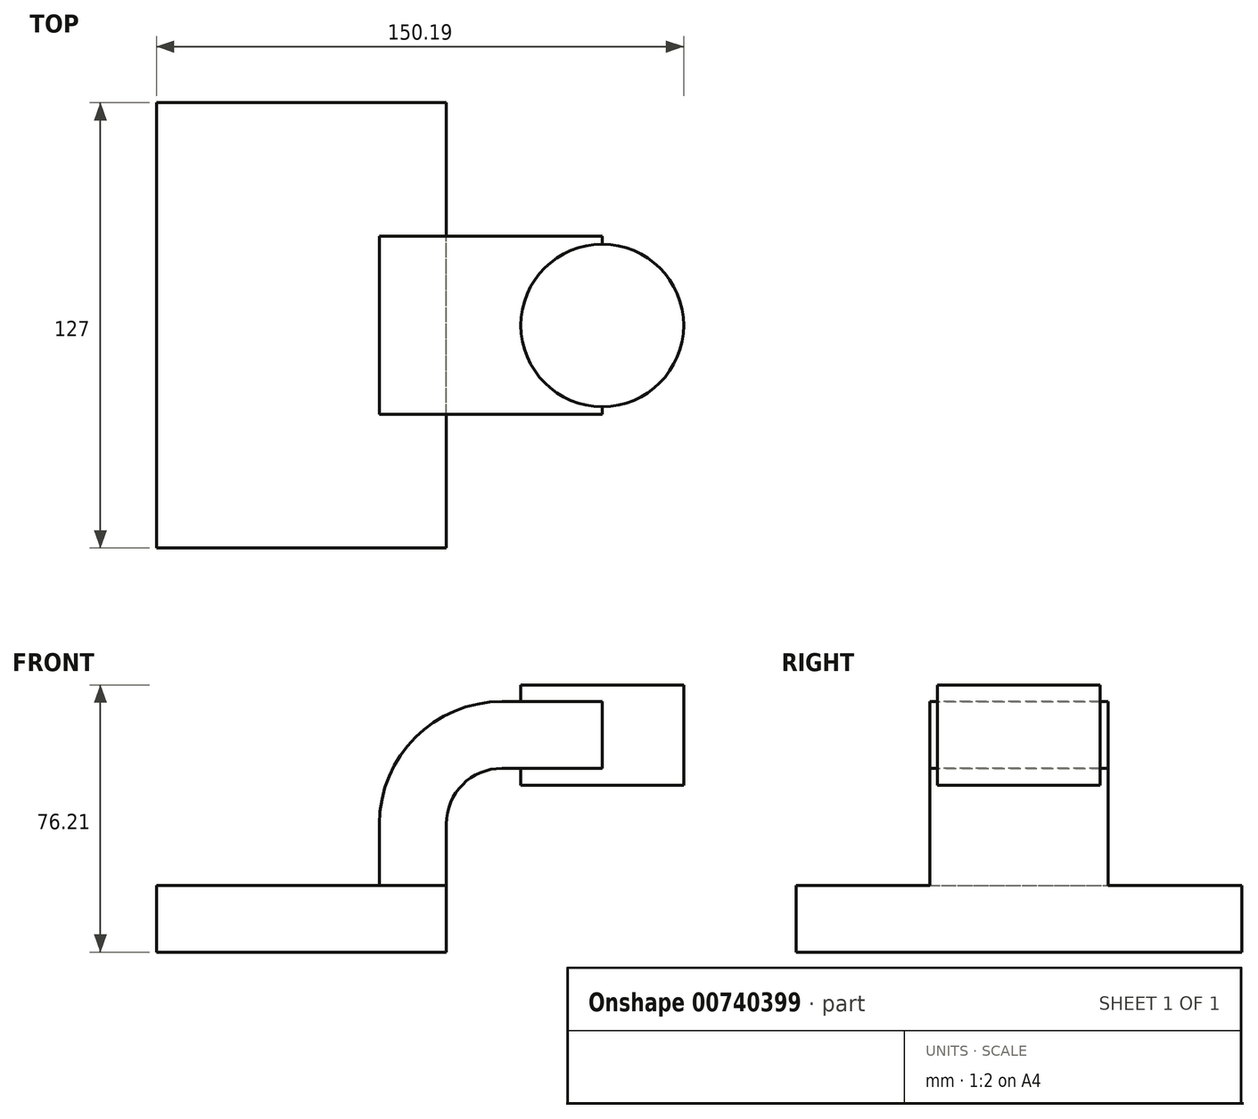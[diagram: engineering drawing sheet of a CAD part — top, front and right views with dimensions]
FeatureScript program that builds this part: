
annotation { "Feature Type Name" : "Feature", "Feature Type Description" : "" }
export const myFeature = defineFeature(function(context is Context, id is Id, definition is map)
    precondition{}
    {
        {
            var Q0;
            Q0=qCreatedBy(makeId("Front.planeOp"),FACE);
            var sketch = newSketch(context, id + "F0", { "sketchPlane" : qUnion([Q0])});
            skLineSegment(sketch, "E0.bottom", {"start": v(-41.28, -9.53) * mm, "end": v(41.28, -9.53) * mm});
            skLineSegment(sketch, "E0.top", {"start": v(-41.28, 9.53) * mm, "end": v(41.28, 9.53) * mm});
            skLineSegment(sketch, "E0.left", {"start": v(-41.28, -9.53) * mm, "end": v(-41.28, 9.53) * mm});
            skLineSegment(sketch, "E0.right", {"start": v(41.28, -9.53) * mm, "end": v(41.28, 9.53) * mm});
            skPoint(sketch, "E0.middle", {"position": v(0, 0) * mm});
            skLineSegment(sketch, "E1.bottom", {"start": v(58.1, 38.1) * mm, "end": v(108.9, 38.1) * mm});
            skLineSegment(sketch, "E1.top", {"start": v(58.1, 66.67) * mm, "end": v(108.9, 66.67) * mm});
            skLineSegment(sketch, "E1.left", {"start": v(58.1, 38.1) * mm, "end": v(58.1, 66.68) * mm});
            skLineSegment(sketch, "E1.right", {"start": v(108.9, 38.1) * mm, "end": v(108.9, 66.67) * mm});
            skPoint(sketch, "E1.middle", {"position": v(83.5, 52.39) * mm});
            skLineSegment(sketch, "E2", {"start": v(41.28, 9.52) * mm, "end": v(41.28, 27) * mm});
            skArc(sketch, "E3", {"start": v(41.27, 27) * mm, "mid": v(45.92, 38.23) * mm, "end": v(57.15, 42.88) * mm});
            skLineSegment(sketch, "E4", {"start": v(57.15, 42.88) * mm, "end": v(85.72, 42.88) * mm});
            skLineSegment(sketch, "E5.0", {"start": v(57.15, 61.93) * mm, "end": v(85.72, 61.93) * mm});
            skArc(sketch, "E5.1", {"start": v(22.22, 27) * mm, "mid": v(32.45, 51.7) * mm, "end": v(57.15, 61.93) * mm});
            skLineSegment(sketch, "E5.2", {"start": v(22.22, 9.52) * mm, "end": v(22.22, 27) * mm});
            skLineSegment(sketch, "E6", {"start": v(85.72, 42.88) * mm, "end": v(85.72, 61.93) * mm});
            skLineSegment(sketch, "E7", {"start": v(85.72, 42.88) * mm, "end": v(85.72, 38.1) * mm});
            skLineSegment(sketch, "E8", {"start": v(85.72, 38.1) * mm, "end": v(85.72, 66.67) * mm});
            skFitSpline(sketch, "E9", {"points": [v(-41.28, 9.53) * mm, v(57.15, 61.93) * mm], "startDerivative": vector(4.43, 54.66) * mm, "endDerivative": vector(148.05, -1.5) * mm});
            skSolve(sketch);
        }
        {
            var Q0;
            Q0=makeQuery(id+"F0.imprint","IMPRINT",FACE,{"disambiguationData":[TD([[makeQuery(id+"F0.imprint","IMPRINT",EDGE,{"derivedFrom":sQuery(id+"F0.wireOp",EDGE,"E0.bottom")}),1.0]])]});
            extrude(context, id + "F1", {"entities" : qUnion([Q0]), "endBound" : BoundingType.SYMMETRIC, "depth" : 127 * mm, "offsetDistance" : 25.4 * mm});
        }
        {
            var Q0;
            {var subQ1=sQuery(id+"F0.wireOp",EDGE,"E2");Q0=makeQuery(id+"F0.imprint","IMPRINT",FACE,{"disambiguationData":[TD([[makeQuery(id+"F0.imprint","IMPRINT",EDGE,{"derivedFrom":subQ1}),1.0]])]});}
            var Q1;
            {var subQ0=sQuery(id+"F0.wireOp",EDGE,"E4");var subQ1=sQuery(id+"F0.wireOp",EDGE,"E1.left");var subQ2=makeQuery(id+"F0.imprint","INTERSECT",VERTEX,{"derivedFrom":[subQ1,subQ0]});Q1=makeQuery(id+"F0.imprint","IMPRINT",FACE,{"disambiguationData":[TD([[makeQuery(id+"F0.imprint","IMPRINT",EDGE,{"disambiguationData":[TD([[subQ2,-1.0]])],"derivedFrom":subQ1}),-1.0]])]});}
            extrude(context, id + "F2", {"entities" : qUnion([Q0, Q1]), "operationType" : NewBodyOperationType.ADD, "endBound" : BoundingType.SYMMETRIC, "depth" : 50.8 * mm, "offsetDistance" : 25.4 * mm});
        }
        {
            var Q0;
            Q0=makeQuery(id+"F0.imprint","IMPRINT",FACE,{"disambiguationData":[TD([[makeQuery(id+"F0.imprint","IMPRINT",EDGE,{"derivedFrom":sQuery(id+"F0.wireOp",EDGE,"E5.1")}),1.0]])]});
            extrude(context, id + "F3", {"entities" : qUnion([Q0]), "operationType" : NewBodyOperationType.ADD, "endBound" : BoundingType.SYMMETRIC, "depth" : 15.88 * mm, "offsetDistance" : 25.4 * mm});
        }
        {
            var Q0;
            {var subQ0=sQuery(id+"F0.wireOp",EDGE,"E1.right");Q0=makeQuery(id+"F0.imprint","IMPRINT",FACE,{"disambiguationData":[TD([[makeQuery(id+"F0.imprint","IMPRINT",EDGE,{"derivedFrom":subQ0}),1.0]])]});}
            var Q1;
            Q1=sQuery(id+"F0.wireOp",EDGE,"E6");
            revolve(context, id + "F4", {"operationType" : NewBodyOperationType.ADD, "surfaceOperationType" : NewSurfaceOperationType.NEW, "entities" : qUnion([Q0]), "axis" : qUnion([Q1]), "revolveType" : RevolveType.FULL});
        }
    });
